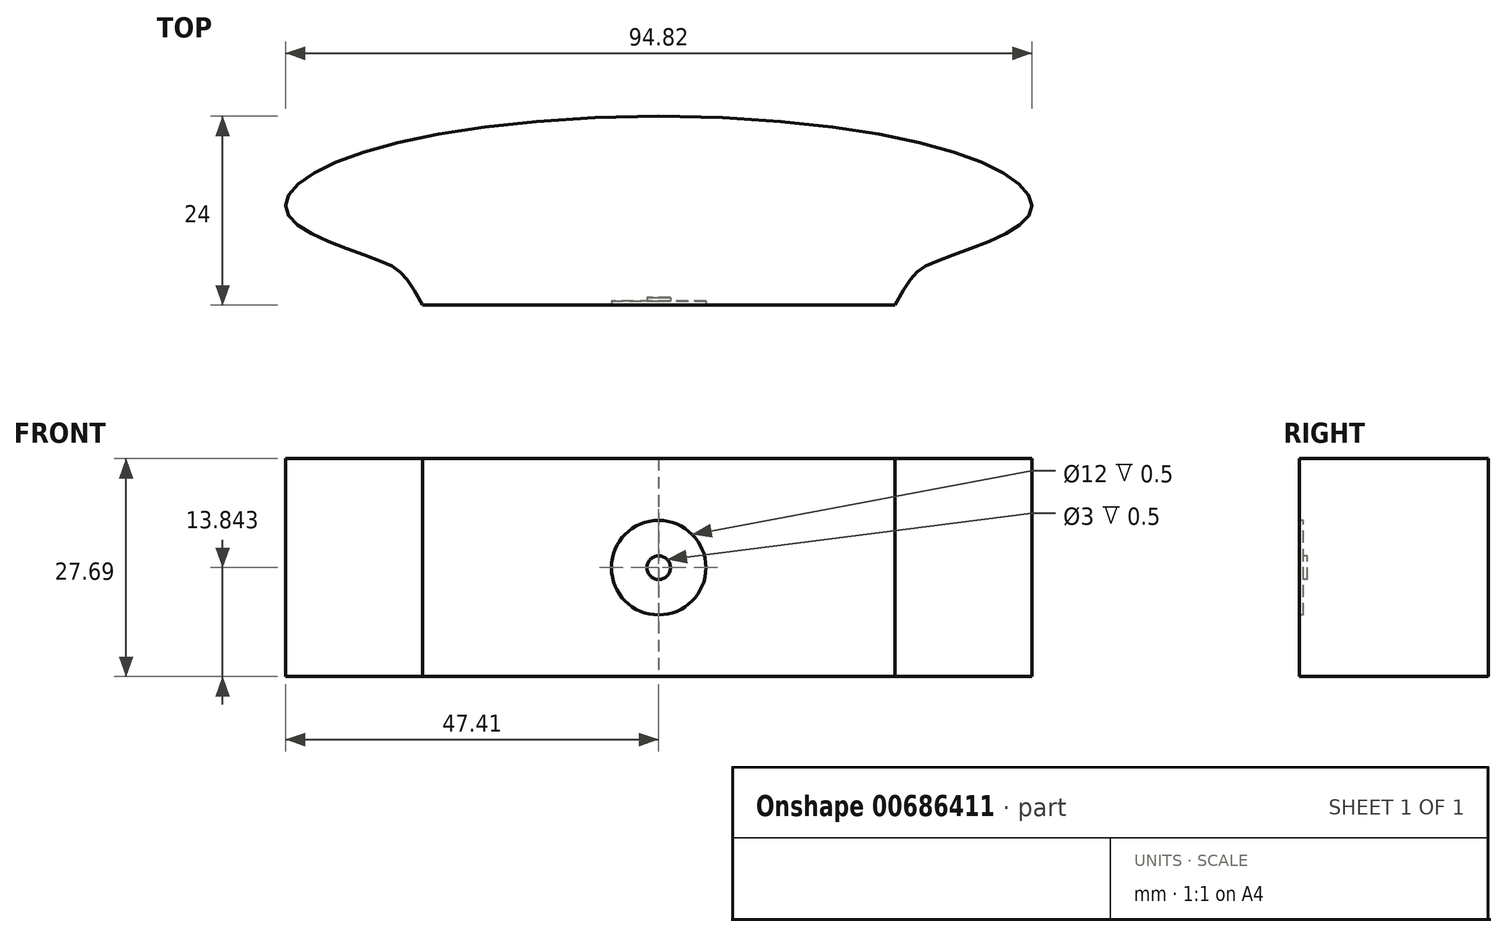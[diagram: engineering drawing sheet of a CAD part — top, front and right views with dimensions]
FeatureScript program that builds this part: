
annotation { "Feature Type Name" : "Feature", "Feature Type Description" : "" }
export const myFeature = defineFeature(function(context is Context, id is Id, definition is map)
    precondition{}
    {
        {
            var Q0;
            Q0=qCreatedBy(makeId("Top.planeOp"),FACE);
            var sketch = newSketch(context, id + "F0", { "sketchPlane" : qUnion([Q0])});
            skLineSegment(sketch, "E0", {"start": v(0, 0) * mm, "end": v(94, 0) * mm, "construction": true});
            skLineSegment(sketch, "E1", {"start": v(47, 0) * mm, "end": v(47, 12.66) * mm, "construction": true});
            skFitSpline(sketch, "E2", {"points": [v(47, 12.66) * mm, v(0, 0) * mm, v(12.26, -6) * mm, v(17, -11.34) * mm], "startDerivative": vector(-195.1, -1.25) * mm, "endDerivative": vector(29.63, -52.55) * mm});
            skLineSegment(sketch, "E3", {"start": v(17, -11.34) * mm, "end": v(47, -11.34) * mm});
            skLineSegment(sketch, "E4.MirrorCS", {"start": v(77, -11.34) * mm, "end": v(47, -11.34) * mm});
            skFitSpline(sketch, "E5.MirrorCS", {"points": [v(47, 12.66) * mm, v(94, 0) * mm, v(81.74, -6) * mm, v(77, -11.34) * mm], "startDerivative": vector(195.1, -1.25) * mm, "endDerivative": vector(-29.63, -52.55) * mm});
            skSolve(sketch);
        }
        {
            var Q0;
            Q0 = qSketchRegion(id + "F0", true);
            extrude(context, id + "F1", {"entities" : qUnion([Q0]), "depth" : 27.7 * mm, "offsetDistance" : 25 * mm});
        }
        {
            var Q0;
            Q0=makeQuery(id+"F1.opExtrude","SWEPT_FACE",FACE,{"disambiguationData":[OSD([sQuery(id+"F0.wireOp",EDGE,"E3"),sQuery(id+"F0.wireOp",EDGE,"E4.MirrorCS")])]});
            var sketch = newSketch(context, id + "F2", { "sketchPlane" : qUnion([Q0])});
            skLineSegment(sketch, "E6", {"start": v(17, 27.69) * mm, "end": v(77, 0) * mm, "construction": true});
            skCircle(sketch, "E7", {"center": v(47, 13.84) * mm, "radius": 1.5 * mm});
            skSolve(sketch);
        }
        {
            var Q0;
            Q0 = qSketchRegion(id + "F2", true);
            extrude(context, id + "F3", {"entities" : qUnion([Q0]), "operationType" : NewBodyOperationType.REMOVE, "oppositeDirection" : true, "depth" : 1 * mm, "offsetDistance" : 25 * mm});
        }
        {
            var Q0;
            Q0=makeQuery(id+"F1.opExtrude","SWEPT_FACE",FACE,{"disambiguationData":[OSD([sQuery(id+"F0.wireOp",EDGE,"E3"),sQuery(id+"F0.wireOp",EDGE,"E4.MirrorCS")])]});
            var sketch = newSketch(context, id + "F4", { "sketchPlane" : qUnion([Q0])});
            skLineSegment(sketch, "E8", {"start": v(31, 13.84) * mm, "end": v(63, 13.84) * mm});
            skPoint(sketch, "E8.startSnap0", {"position": v(17, 13.84) * mm});
            skLineSegment(sketch, "E9", {"start": v(47, 27.69) * mm, "end": v(47, 13.84) * mm, "construction": true});
            skArc(sketch, "E10.0.startCap", {"start": v(31, 2.84) * mm, "mid": v(20, 13.84) * mm, "end": v(31, 24.84) * mm, "construction": true});
            skArc(sketch, "E10.0.endCap", {"start": v(63, 24.84) * mm, "mid": v(74, 13.84) * mm, "end": v(63, 2.84) * mm, "construction": true});
            skLineSegment(sketch, "E10.0.left", {"start": v(31, 24.84) * mm, "end": v(63, 24.84) * mm});
            skLineSegment(sketch, "E10.0.right", {"start": v(31, 2.84) * mm, "end": v(63, 2.84) * mm});
            skSolve(sketch);
        }
        {
            var Q0;
            {var subQ1=sQuery(id+"F0.wireOp",EDGE,"E3");Q0=makeQuery(id+"F4.imprint","IMPRINT",FACE,{"disambiguationData":[TD([[makeQuery(id+"F4.imprint","IMPRINT",EDGE,{"derivedFrom":makeQuery(id+"F1.opExtrude","SWEPT_EDGE",EDGE,{"disambiguationData":[OSD([sQuery(id+"F0.wireOp",EDGE,"E2"),subQ1])]})}),1.0]])]});}
            var sketch = newSketch(context, id + "F5", { "sketchPlane" : qUnion([Q0])});
            skCircle(sketch, "E11", {"center": v(47, 13.84) * mm, "radius": 6 * mm});
            skSolve(sketch);
        }
        {
            var Q0;
            Q0 = qSketchRegion(id + "F5", true);
            extrude(context, id + "F6", {"entities" : qUnion([Q0]), "operationType" : NewBodyOperationType.REMOVE, "oppositeDirection" : true, "depth" : .5 * mm, "offsetDistance" : 25 * mm});
        }
    });
